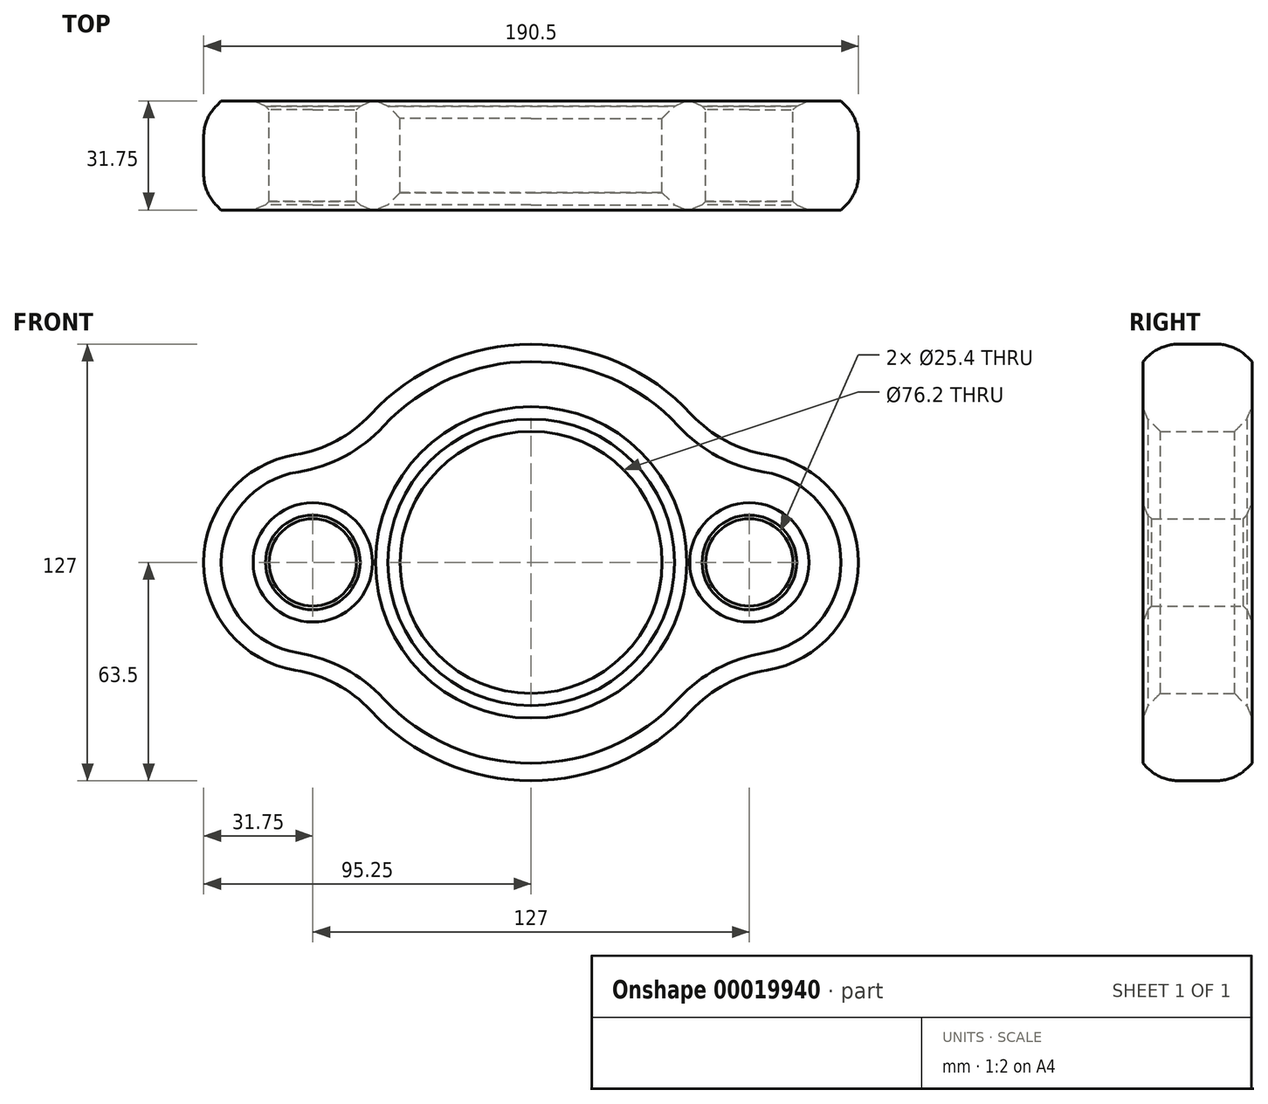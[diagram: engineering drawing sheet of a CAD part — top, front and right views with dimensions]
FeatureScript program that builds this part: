
annotation { "Feature Type Name" : "Feature", "Feature Type Description" : "" }
export const myFeature = defineFeature(function(context is Context, id is Id, definition is map)
    precondition{}
    {
        {
            var Q0;
            Q0=qCreatedBy(makeId("Front.planeOp"),FACE);
            var sketch = newSketch(context, id + "F0", { "sketchPlane" : qUnion([Q0])});
            skArc(sketch, "E0", {"start": v(-46.63, -43.1) * mm, "mid": v(0, -63.5) * mm, "end": v(46.63, -43.1) * mm});
            skArc(sketch, "E1", {"start": v(-68.55, 31.35) * mm, "mid": v(-95.25, 0) * mm, "end": v(-68.55, -31.35) * mm});
            skArc(sketch, "E2", {"start": v(68.55, -31.35) * mm, "mid": v(95.25, 0) * mm, "end": v(68.55, 31.35) * mm});
            skCircle(sketch, "E3", {"center": v(63.5, 0) * mm, "radius": 12.7 * mm});
            skCircle(sketch, "E4", {"center": v(-63.5, 0) * mm, "radius": 12.7 * mm});
            skCircle(sketch, "E5", {"center": v(0, 0) * mm, "radius": 38.1 * mm});
            skArc(sketch, "E6.trimOffspring", {"start": v(46.63, 43.1) * mm, "mid": v(0, 63.5) * mm, "end": v(-46.63, 43.1) * mm});
            skPoint(sketch, "E7.visualSharp", {"position": v(-55.56, 30.74) * mm});
            skArc(sketch, "E7.filletArc", {"start": v(-68.55, 31.35) * mm, "mid": v(-56.6, 35.38) * mm, "end": v(-46.63, 43.1) * mm});
            skPoint(sketch, "E8.visualSharp", {"position": v(55.56, 30.74) * mm});
            skArc(sketch, "E8.filletArc", {"start": v(46.63, 43.1) * mm, "mid": v(56.6, 35.38) * mm, "end": v(68.55, 31.35) * mm});
            skPoint(sketch, "E9.visualSharp", {"position": v(55.56, -30.74) * mm});
            skArc(sketch, "E9.filletArc", {"start": v(68.55, -31.35) * mm, "mid": v(56.6, -35.38) * mm, "end": v(46.63, -43.1) * mm});
            skPoint(sketch, "E10.visualSharp", {"position": v(-55.56, -30.74) * mm});
            skArc(sketch, "E10.filletArc", {"start": v(-46.63, -43.1) * mm, "mid": v(-56.6, -35.38) * mm, "end": v(-68.55, -31.35) * mm});
            skSolve(sketch);
        }
        {
            var Q0;
            Q0 = qSketchRegion(id + "F0", true);
            extrude(context, id + "F1", {"entities" : qUnion([Q0]), "depth" : 31.75 * mm});
        }
        {
            var Q0;
            Q0=makeQuery(id+"F1.opExtrude","SWEPT_FACE",FACE,{"disambiguationData":[OSD([sQuery(id+"F0.wireOp",EDGE,"E5")])]});
            chamfer(context, id + "F2", {"entities" : qUnion([Q0]), "width" : 5.08 * mm, "tangentPropagation" : true});
        }
        {
            var Q0;
            Q0=makeQuery(id+"F1.opExtrude","SWEPT_FACE",FACE,{"disambiguationData":[OSD([sQuery(id+"F0.wireOp",EDGE,"E4")])]});
            var Q1;
            Q1=makeQuery(id+"F1.opExtrude","SWEPT_FACE",FACE,{"disambiguationData":[OSD([sQuery(id+"F0.wireOp",EDGE,"E3")])]});
            chamfer(context, id + "F3", {"entities" : qUnion([Q0, Q1]), "width" : 2.54 * mm, "tangentPropagation" : true});
        }
        {
            var Q0;
            Q0=makeQuery(id+"F1.opExtrude","CAP_FACE",FACE,{"disambiguationData":[OSD([sQuery(id+"F0.wireOp",EDGE,"E0"),sQuery(id+"F0.wireOp",EDGE,"E1"),sQuery(id+"F0.wireOp",EDGE,"E2"),sQuery(id+"F0.wireOp",EDGE,"E3"),sQuery(id+"F0.wireOp",EDGE,"E4"),sQuery(id+"F0.wireOp",EDGE,"E5"),sQuery(id+"F0.wireOp",EDGE,"E6.trimOffspring"),sQuery(id+"F0.wireOp",EDGE,"E7.filletArc"),sQuery(id+"F0.wireOp",EDGE,"E8.filletArc"),sQuery(id+"F0.wireOp",EDGE,"E9.filletArc"),sQuery(id+"F0.wireOp",EDGE,"E10.filletArc")])],"isStart":true});
            chamfer(context, id + "F4", {"entities" : qUnion([Q0]), "width" : 5.08 * mm, "tangentPropagation" : true});
        }
        {
            var Q0;
            Q0=makeQuery(id+"F1.opExtrude","CAP_FACE",FACE,{"disambiguationData":[OSD([sQuery(id+"F0.wireOp",EDGE,"E0"),sQuery(id+"F0.wireOp",EDGE,"E1"),sQuery(id+"F0.wireOp",EDGE,"E2"),sQuery(id+"F0.wireOp",EDGE,"E3"),sQuery(id+"F0.wireOp",EDGE,"E4"),sQuery(id+"F0.wireOp",EDGE,"E5"),sQuery(id+"F0.wireOp",EDGE,"E6.trimOffspring"),sQuery(id+"F0.wireOp",EDGE,"E7.filletArc"),sQuery(id+"F0.wireOp",EDGE,"E8.filletArc"),sQuery(id+"F0.wireOp",EDGE,"E9.filletArc"),sQuery(id+"F0.wireOp",EDGE,"E10.filletArc")])],"isStart":false});
            chamfer(context, id + "F5", {"entities" : qUnion([Q0]), "width" : 5.08 * mm, "tangentPropagation" : true});
        }
        {
            var Q0;
            {var subQ0=sQuery(id+"F0.wireOp",EDGE,"E7.filletArc");Q0=makeQuery(id+"F4.opChamfer","BLEND_EDGE",EDGE,{"blendedFrom":[makeQuery(id+"F1.opExtrude","CAP_EDGE",EDGE,{"disambiguationData":[OSD([subQ0])],"isStart":true}),makeQuery(id+"F1.opExtrude","SWEPT_FACE",FACE,{"disambiguationData":[OSD([subQ0])]})],"blendedInto":[makeQuery(id+"F1.opExtrude","SWEPT_FACE",FACE,{"disambiguationData":[OSD([subQ0])]})]});}
            var Q1;
            {var subQ0=sQuery(id+"F0.wireOp",EDGE,"E7.filletArc");Q1=makeQuery(id+"F5.opChamfer","BLEND_EDGE",EDGE,{"blendedFrom":[makeQuery(id+"F1.opExtrude","CAP_EDGE",EDGE,{"disambiguationData":[OSD([subQ0])],"isStart":false}),makeQuery(id+"F1.opExtrude","SWEPT_FACE",FACE,{"disambiguationData":[OSD([subQ0])]})],"blendedInto":[makeQuery(id+"F1.opExtrude","SWEPT_FACE",FACE,{"disambiguationData":[OSD([subQ0])]})]});}
            var Q2;
            {var subQ0=sQuery(id+"F0.wireOp",EDGE,"E1");Q2=makeQuery(id+"F5.opChamfer","BLEND_EDGE",EDGE,{"blendedFrom":[makeQuery(id+"F1.opExtrude","CAP_EDGE",EDGE,{"disambiguationData":[OSD([subQ0])],"isStart":false}),makeQuery(id+"F1.opExtrude","SWEPT_FACE",FACE,{"disambiguationData":[OSD([subQ0])]})],"blendedInto":[makeQuery(id+"F1.opExtrude","SWEPT_FACE",FACE,{"disambiguationData":[OSD([subQ0])]})]});}
            var Q3;
            {var subQ0=sQuery(id+"F0.wireOp",EDGE,"E1");Q3=makeQuery(id+"F4.opChamfer","BLEND_EDGE",EDGE,{"blendedFrom":[makeQuery(id+"F1.opExtrude","CAP_EDGE",EDGE,{"disambiguationData":[OSD([subQ0])],"isStart":true}),makeQuery(id+"F1.opExtrude","SWEPT_FACE",FACE,{"disambiguationData":[OSD([subQ0])]})],"blendedInto":[makeQuery(id+"F1.opExtrude","SWEPT_FACE",FACE,{"disambiguationData":[OSD([subQ0])]})]});}
            var Q4;
            {var subQ0=sQuery(id+"F0.wireOp",EDGE,"E6.trimOffspring");Q4=makeQuery(id+"F5.opChamfer","BLEND_EDGE",EDGE,{"blendedFrom":[makeQuery(id+"F1.opExtrude","CAP_EDGE",EDGE,{"disambiguationData":[OSD([subQ0])],"isStart":false}),makeQuery(id+"F1.opExtrude","SWEPT_FACE",FACE,{"disambiguationData":[OSD([subQ0])]})],"blendedInto":[makeQuery(id+"F1.opExtrude","SWEPT_FACE",FACE,{"disambiguationData":[OSD([subQ0])]})]});}
            var Q5;
            {var subQ0=sQuery(id+"F0.wireOp",EDGE,"E6.trimOffspring");Q5=makeQuery(id+"F4.opChamfer","BLEND_EDGE",EDGE,{"blendedFrom":[makeQuery(id+"F1.opExtrude","CAP_EDGE",EDGE,{"disambiguationData":[OSD([subQ0])],"isStart":true}),makeQuery(id+"F1.opExtrude","SWEPT_FACE",FACE,{"disambiguationData":[OSD([subQ0])]})],"blendedInto":[makeQuery(id+"F1.opExtrude","SWEPT_FACE",FACE,{"disambiguationData":[OSD([subQ0])]})]});}
            var Q6;
            {var subQ0=sQuery(id+"F0.wireOp",EDGE,"E8.filletArc");Q6=makeQuery(id+"F5.opChamfer","BLEND_EDGE",EDGE,{"blendedFrom":[makeQuery(id+"F1.opExtrude","CAP_EDGE",EDGE,{"disambiguationData":[OSD([subQ0])],"isStart":false}),makeQuery(id+"F1.opExtrude","SWEPT_FACE",FACE,{"disambiguationData":[OSD([subQ0])]})],"blendedInto":[makeQuery(id+"F1.opExtrude","SWEPT_FACE",FACE,{"disambiguationData":[OSD([subQ0])]})]});}
            var Q7;
            {var subQ0=sQuery(id+"F0.wireOp",EDGE,"E8.filletArc");Q7=makeQuery(id+"F4.opChamfer","BLEND_EDGE",EDGE,{"blendedFrom":[makeQuery(id+"F1.opExtrude","CAP_EDGE",EDGE,{"disambiguationData":[OSD([subQ0])],"isStart":true}),makeQuery(id+"F1.opExtrude","SWEPT_FACE",FACE,{"disambiguationData":[OSD([subQ0])]})],"blendedInto":[makeQuery(id+"F1.opExtrude","SWEPT_FACE",FACE,{"disambiguationData":[OSD([subQ0])]})]});}
            var Q8;
            {var subQ0=sQuery(id+"F0.wireOp",EDGE,"E2");Q8=makeQuery(id+"F4.opChamfer","BLEND_EDGE",EDGE,{"blendedFrom":[makeQuery(id+"F1.opExtrude","CAP_EDGE",EDGE,{"disambiguationData":[OSD([subQ0])],"isStart":true}),makeQuery(id+"F1.opExtrude","SWEPT_FACE",FACE,{"disambiguationData":[OSD([subQ0])]})],"blendedInto":[makeQuery(id+"F1.opExtrude","SWEPT_FACE",FACE,{"disambiguationData":[OSD([subQ0])]})]});}
            var Q9;
            {var subQ0=sQuery(id+"F0.wireOp",EDGE,"E2");Q9=makeQuery(id+"F5.opChamfer","BLEND_EDGE",EDGE,{"blendedFrom":[makeQuery(id+"F1.opExtrude","CAP_EDGE",EDGE,{"disambiguationData":[OSD([subQ0])],"isStart":false}),makeQuery(id+"F1.opExtrude","SWEPT_FACE",FACE,{"disambiguationData":[OSD([subQ0])]})],"blendedInto":[makeQuery(id+"F1.opExtrude","SWEPT_FACE",FACE,{"disambiguationData":[OSD([subQ0])]})]});}
            var Q10;
            {var subQ0=sQuery(id+"F0.wireOp",EDGE,"E9.filletArc");Q10=makeQuery(id+"F4.opChamfer","BLEND_EDGE",EDGE,{"blendedFrom":[makeQuery(id+"F1.opExtrude","CAP_EDGE",EDGE,{"disambiguationData":[OSD([subQ0])],"isStart":true}),makeQuery(id+"F1.opExtrude","SWEPT_FACE",FACE,{"disambiguationData":[OSD([subQ0])]})],"blendedInto":[makeQuery(id+"F1.opExtrude","SWEPT_FACE",FACE,{"disambiguationData":[OSD([subQ0])]})]});}
            var Q11;
            {var subQ0=sQuery(id+"F0.wireOp",EDGE,"E9.filletArc");Q11=makeQuery(id+"F5.opChamfer","BLEND_EDGE",EDGE,{"blendedFrom":[makeQuery(id+"F1.opExtrude","CAP_EDGE",EDGE,{"disambiguationData":[OSD([subQ0])],"isStart":false}),makeQuery(id+"F1.opExtrude","SWEPT_FACE",FACE,{"disambiguationData":[OSD([subQ0])]})],"blendedInto":[makeQuery(id+"F1.opExtrude","SWEPT_FACE",FACE,{"disambiguationData":[OSD([subQ0])]})]});}
            var Q12;
            {var subQ0=sQuery(id+"F0.wireOp",EDGE,"E0");Q12=makeQuery(id+"F4.opChamfer","BLEND_EDGE",EDGE,{"blendedFrom":[makeQuery(id+"F1.opExtrude","CAP_EDGE",EDGE,{"disambiguationData":[OSD([subQ0])],"isStart":true}),makeQuery(id+"F1.opExtrude","SWEPT_FACE",FACE,{"disambiguationData":[OSD([subQ0])]})],"blendedInto":[makeQuery(id+"F1.opExtrude","SWEPT_FACE",FACE,{"disambiguationData":[OSD([subQ0])]})]});}
            var Q13;
            {var subQ0=sQuery(id+"F0.wireOp",EDGE,"E0");Q13=makeQuery(id+"F5.opChamfer","BLEND_EDGE",EDGE,{"blendedFrom":[makeQuery(id+"F1.opExtrude","CAP_EDGE",EDGE,{"disambiguationData":[OSD([subQ0])],"isStart":false}),makeQuery(id+"F1.opExtrude","SWEPT_FACE",FACE,{"disambiguationData":[OSD([subQ0])]})],"blendedInto":[makeQuery(id+"F1.opExtrude","SWEPT_FACE",FACE,{"disambiguationData":[OSD([subQ0])]})]});}
            var Q14;
            {var subQ0=sQuery(id+"F0.wireOp",EDGE,"E10.filletArc");Q14=makeQuery(id+"F4.opChamfer","BLEND_EDGE",EDGE,{"blendedFrom":[makeQuery(id+"F1.opExtrude","CAP_EDGE",EDGE,{"disambiguationData":[OSD([subQ0])],"isStart":true}),makeQuery(id+"F1.opExtrude","SWEPT_FACE",FACE,{"disambiguationData":[OSD([subQ0])]})],"blendedInto":[makeQuery(id+"F1.opExtrude","SWEPT_FACE",FACE,{"disambiguationData":[OSD([subQ0])]})]});}
            var Q15;
            {var subQ0=sQuery(id+"F0.wireOp",EDGE,"E10.filletArc");Q15=makeQuery(id+"F5.opChamfer","BLEND_EDGE",EDGE,{"blendedFrom":[makeQuery(id+"F1.opExtrude","CAP_EDGE",EDGE,{"disambiguationData":[OSD([subQ0])],"isStart":false}),makeQuery(id+"F1.opExtrude","SWEPT_FACE",FACE,{"disambiguationData":[OSD([subQ0])]})],"blendedInto":[makeQuery(id+"F1.opExtrude","SWEPT_FACE",FACE,{"disambiguationData":[OSD([subQ0])]})]});}
            fillet(context, id + "F6", {"entities" : qUnion([Q0, Q1, Q2, Q3, Q4, Q5, Q6, Q7, Q8, Q9, Q10, Q11, Q12, Q13, Q14, Q15]), "radius" : 12.7 * mm, "tangentPropagation" : true, "allowEdgeOverflow" : false});
        }
    });
